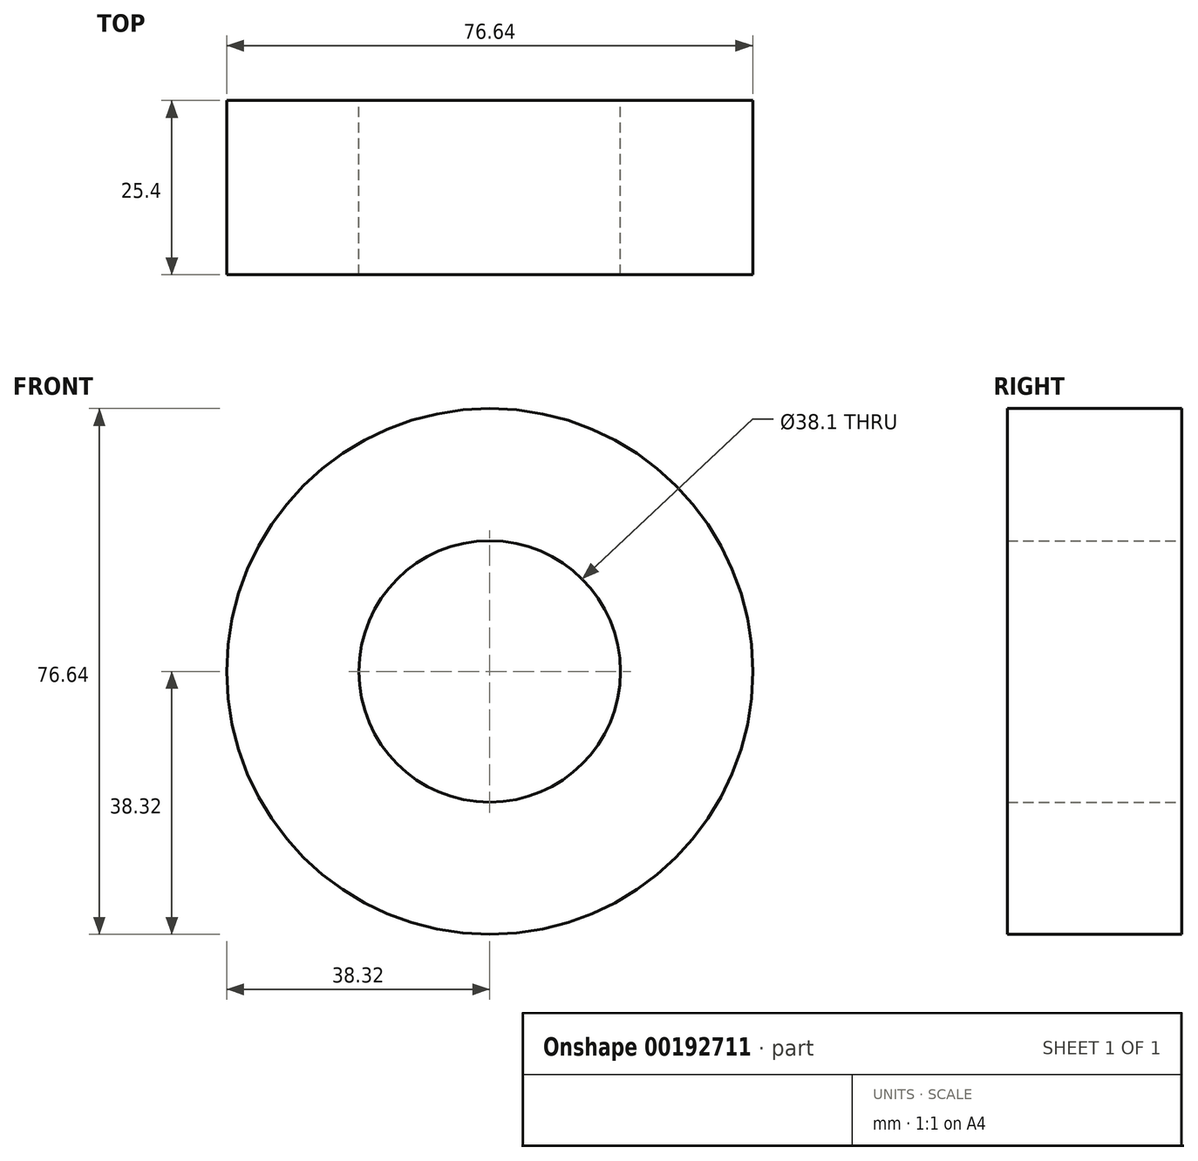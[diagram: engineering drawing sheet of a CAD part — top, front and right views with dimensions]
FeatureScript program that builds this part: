
annotation { "Feature Type Name" : "Feature", "Feature Type Description" : "" }
export const myFeature = defineFeature(function(context is Context, id is Id, definition is map)
    precondition{}
    {
        {
            var Q0;
            Q0=qCreatedBy(makeId("Front.planeOp"),FACE);
            var sketch = newSketch(context, id + "F0", { "sketchPlane" : qUnion([Q0])});
            skCircle(sketch, "E0", {"center": v(0, 0) * mm, "radius": 19.05 * mm});
            skCircle(sketch, "E1", {"center": v(0, 0) * mm, "radius": 38.32 * mm});
            skSolve(sketch);
        }
        {
            var Q0;
            Q0=makeQuery(id+"F0.imprint","IMPRINT",FACE,{"disambiguationData":[TD([[makeQuery(id+"F0.imprint","IMPRINT",EDGE,{"derivedFrom":sQuery(id+"F0.wireOp",EDGE,"E0")}),-1.0]])]});
            extrude(context, id + "F1", {"entities" : qUnion([Q0]), "depth" : 25.4 * mm});
        }
    });
